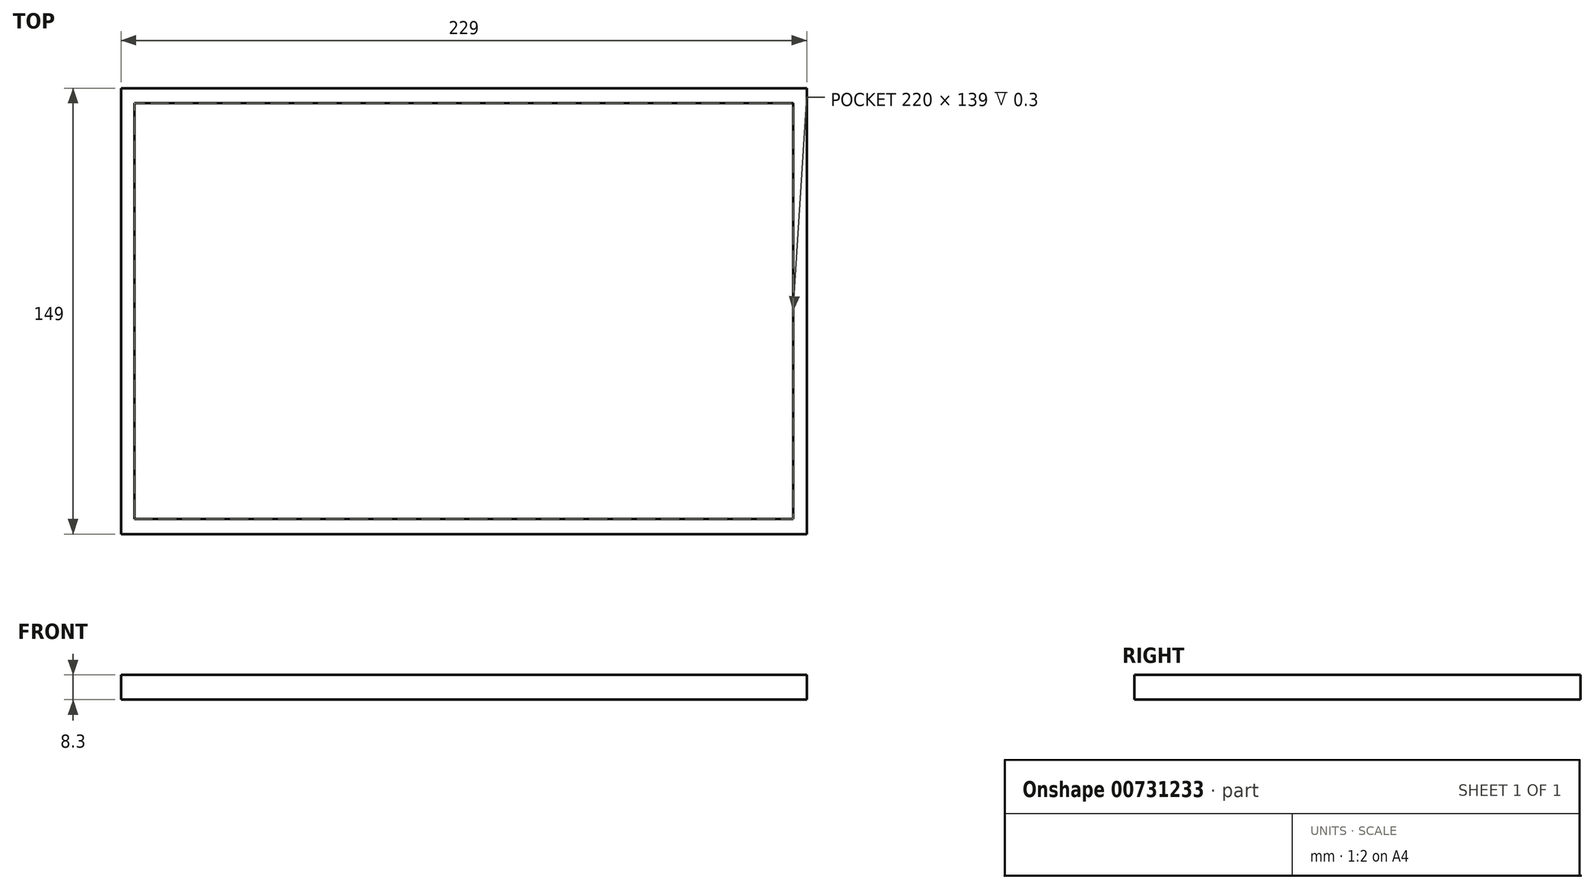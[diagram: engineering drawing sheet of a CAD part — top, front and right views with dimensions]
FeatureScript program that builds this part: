
annotation { "Feature Type Name" : "Feature", "Feature Type Description" : "" }
export const myFeature = defineFeature(function(context is Context, id is Id, definition is map)
    precondition{}
    {
        {
            var Q0;
            Q0=qCreatedBy(makeId("Top.planeOp"),FACE);
            var sketch = newSketch(context, id + "F0", { "sketchPlane" : qUnion([Q0])});
            skLineSegment(sketch, "E0.bottom", {"start": v(110, 69.5) * mm, "end": v(-110, 69.5) * mm});
            skLineSegment(sketch, "E0.top", {"start": v(110, -69.5) * mm, "end": v(-110, -69.5) * mm});
            skLineSegment(sketch, "E0.left", {"start": v(110, 69.5) * mm, "end": v(110, -69.5) * mm});
            skLineSegment(sketch, "E0.right", {"start": v(-110, 69.5) * mm, "end": v(-110, -69.5) * mm});
            skPoint(sketch, "E0.middle", {"position": v(0, 0) * mm});
            skLineSegment(sketch, "E1.bottom", {"start": v(114.5, 74.5) * mm, "end": v(-114.5, 74.5) * mm});
            skLineSegment(sketch, "E1.top", {"start": v(114.5, -74.5) * mm, "end": v(-114.5, -74.5) * mm});
            skLineSegment(sketch, "E1.left", {"start": v(114.5, 74.5) * mm, "end": v(114.5, -74.5) * mm});
            skLineSegment(sketch, "E1.right", {"start": v(-114.5, 74.5) * mm, "end": v(-114.5, -74.5) * mm});
            skSolve(sketch);
        }
        {
            var Q0;
            Q0=makeQuery(id+"F0.imprint","IMPRINT",FACE,{"disambiguationData":[TD([[makeQuery(id+"F0.imprint","IMPRINT",EDGE,{"derivedFrom":sQuery(id+"F0.wireOp",EDGE,"E0.bottom")}),1.0]])]});
            extrude(context, id + "F1", {"entities" : qUnion([Q0]), "oppositeDirection" : true, "depth" : (8) * mm, "offsetDistance" : 25 * mm});
        }
        {
            var Q0;
            Q0=makeQuery(id+"F0.imprint","IMPRINT",FACE,{"disambiguationData":[TD([[makeQuery(id+"F0.imprint","IMPRINT",EDGE,{"derivedFrom":sQuery(id+"F0.wireOp",EDGE,"E0.bottom")}),-1.0]])]});
            var Q1;
            Q1=makeQuery(id+"F1.opExtrude","CAP_FACE",FACE,{"disambiguationData":[OSD([sQuery(id+"F0.wireOp",EDGE,"E0.bottom"),sQuery(id+"F0.wireOp",EDGE,"E0.top"),sQuery(id+"F0.wireOp",EDGE,"E0.left"),sQuery(id+"F0.wireOp",EDGE,"E0.right")])],"isStart":false});
            extrude(context, id + "F2", {"entities" : qUnion([Q0]), "operationType" : NewBodyOperationType.ADD, "depth" : .3 * mm, "offsetDistance" : 25 * mm, "hasSecondDirection" : true, "secondDirectionBound" : SecondDirectionBoundingType.UP_TO_SURFACE, "secondDirectionOppositeDirection" : true, "secondDirectionDepth" : 8 * mm, "secondDirectionBoundEntityFace" : qUnion([Q1])});
        }
    });
